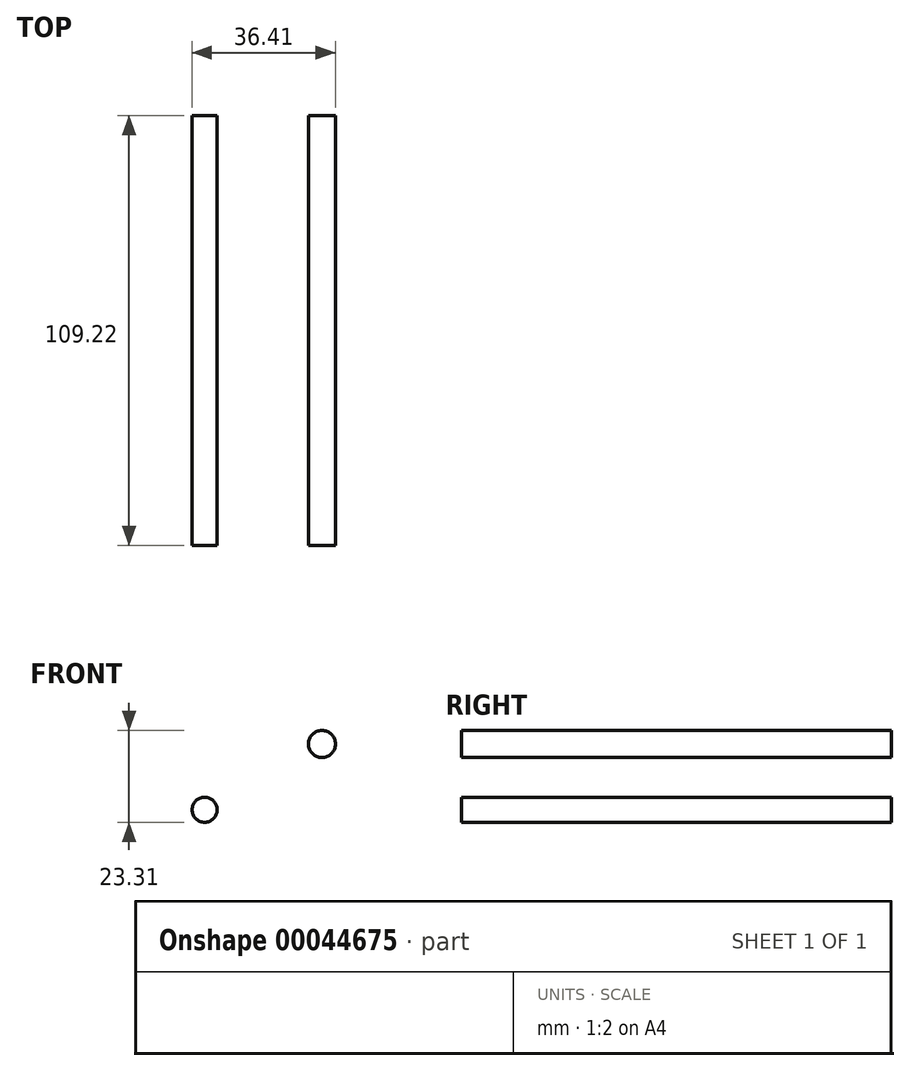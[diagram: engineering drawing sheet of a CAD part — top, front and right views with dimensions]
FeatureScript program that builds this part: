
annotation { "Feature Type Name" : "Feature", "Feature Type Description" : "" }
export const myFeature = defineFeature(function(context is Context, id is Id, definition is map)
    precondition{}
    {
        {
            var Q0;
            Q0=qCreatedBy(makeId("Front.planeOp"),FACE);
            var sketch = newSketch(context, id + "F0", { "sketchPlane" : qUnion([Q0])});
            skCircle(sketch, "E0", {"center": v(-19.36, 44.7) * mm, "radius": 3.43 * mm});
            skCircle(sketch, "E1", {"center": v(-49.16, 28) * mm, "radius": 3.18 * mm});
            skSolve(sketch);
        }
        {
            var Q0;
            Q0 = qSketchRegion(id + "F0", true);
            extrude(context, id + "F1", {"entities" : qUnion([Q0]), "endBound" : BoundingType.SYMMETRIC, "depth" : 109.22 * mm});
        }
    });
